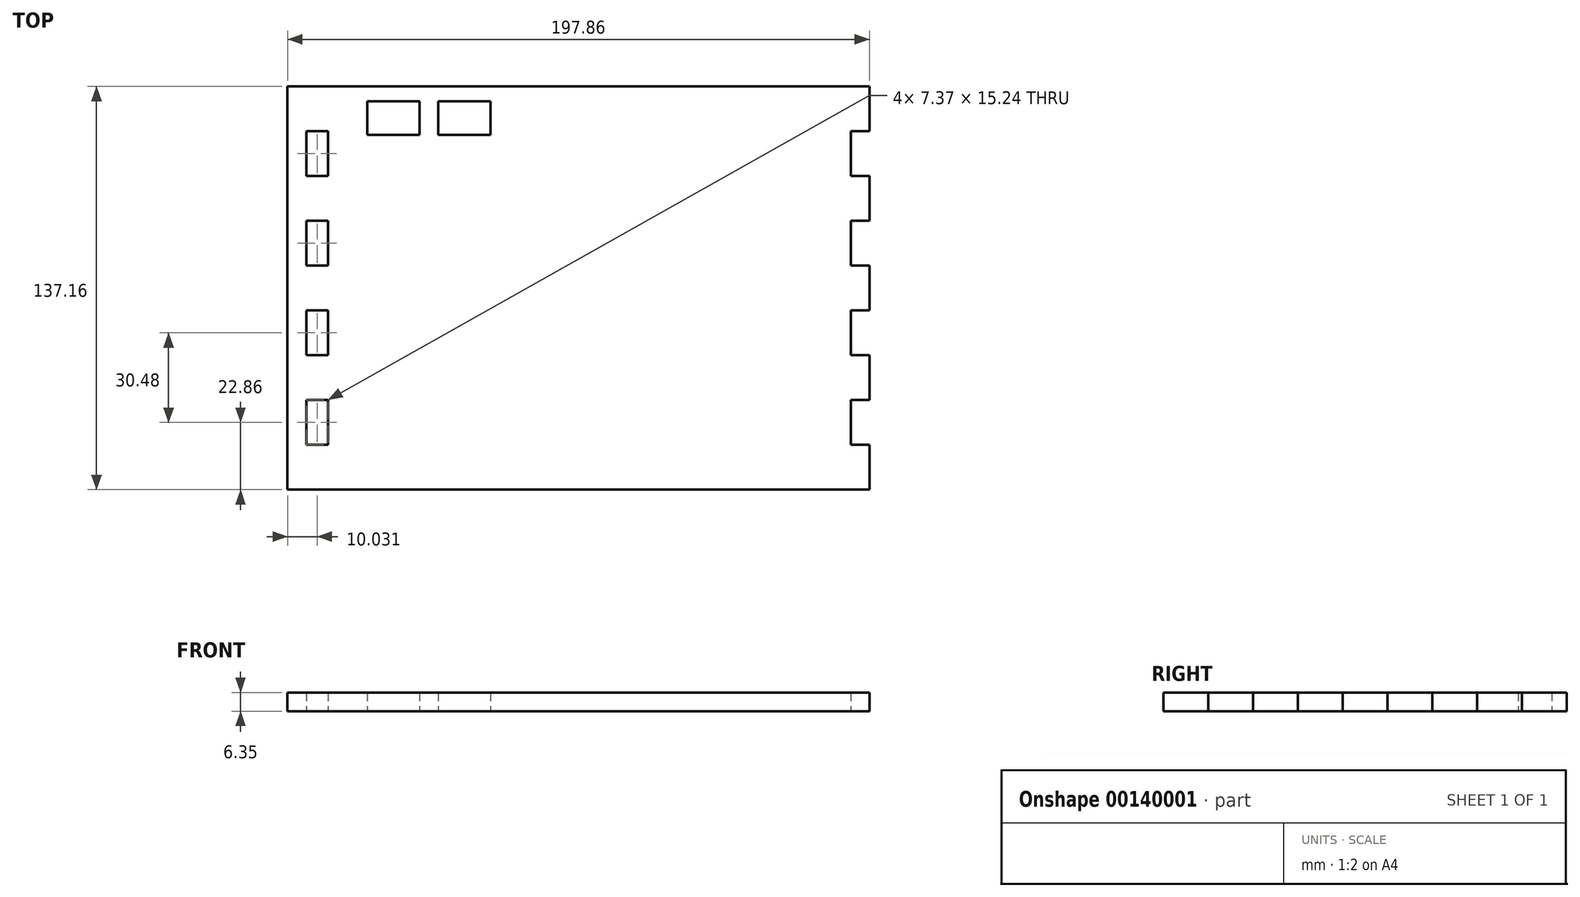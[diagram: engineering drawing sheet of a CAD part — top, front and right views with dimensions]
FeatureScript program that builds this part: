
annotation { "Feature Type Name" : "Feature", "Feature Type Description" : "" }
export const myFeature = defineFeature(function(context is Context, id is Id, definition is map)
    precondition{}
    {
        {
            var Q0;
            Q0=qCreatedBy(makeId("Top.planeOp"),FACE);
            var sketch = newSketch(context, id + "F0", { "sketchPlane" : qUnion([Q0])});
            skLineSegment(sketch, "E0.bottom", {"start": v(-69.3, 76.2) * mm, "end": v(108.5, 76.2) * mm});
            skLineSegment(sketch, "E0.top", {"start": v(-69.3, -60.96) * mm, "end": v(108.46, -60.96) * mm});
            skLineSegment(sketch, "E1", {"start": v(-76.67, 60.96) * mm, "end": v(-69.3, 60.96) * mm});
            skLineSegment(sketch, "E2", {"start": v(-69.3, 60.96) * mm, "end": v(-69.3, 45.72) * mm});
            skLineSegment(sketch, "E3", {"start": v(-69.3, 45.72) * mm, "end": v(-76.67, 45.72) * mm});
            skLineSegment(sketch, "E4", {"start": v(-76.67, 30.48) * mm, "end": v(-69.3, 30.48) * mm});
            skLineSegment(sketch, "E5", {"start": v(-69.3, 30.48) * mm, "end": v(-69.3, 15.24) * mm});
            skLineSegment(sketch, "E6", {"start": v(-69.3, 15.24) * mm, "end": v(-76.67, 15.24) * mm});
            skLineSegment(sketch, "E7", {"start": v(-76.67, 0) * mm, "end": v(-69.3, 0) * mm});
            skLineSegment(sketch, "E8", {"start": v(-69.3, 0) * mm, "end": v(-69.3, -15.24) * mm});
            skLineSegment(sketch, "E9", {"start": v(-69.3, -15.24) * mm, "end": v(-76.67, -15.24) * mm});
            skLineSegment(sketch, "E10", {"start": v(-76.67, -30.48) * mm, "end": v(-69.3, -30.48) * mm});
            skLineSegment(sketch, "E11", {"start": v(-69.3, -30.48) * mm, "end": v(-69.3, -45.72) * mm});
            skLineSegment(sketch, "E12", {"start": v(-69.3, -45.72) * mm, "end": v(-76.67, -45.72) * mm});
            skLineSegment(sketch, "E13", {"start": v(108.5, 76.2) * mm, "end": v(114.84, 76.2) * mm});
            skLineSegment(sketch, "E14", {"start": v(114.84, 76.2) * mm, "end": v(114.84, 60.96) * mm});
            skLineSegment(sketch, "E15", {"start": v(114.84, 60.96) * mm, "end": v(108.5, 60.96) * mm});
            skLineSegment(sketch, "E16", {"start": v(108.5, 60.96) * mm, "end": v(108.5, 45.72) * mm});
            skLineSegment(sketch, "E17", {"start": v(108.5, 45.72) * mm, "end": v(114.84, 45.72) * mm});
            skLineSegment(sketch, "E18", {"start": v(114.84, 45.72) * mm, "end": v(114.84, 30.48) * mm});
            skLineSegment(sketch, "E19", {"start": v(114.84, 30.48) * mm, "end": v(108.5, 30.48) * mm});
            skLineSegment(sketch, "E20", {"start": v(108.5, 30.48) * mm, "end": v(108.5, 15.24) * mm});
            skLineSegment(sketch, "E21", {"start": v(108.5, 15.24) * mm, "end": v(114.84, 15.24) * mm});
            skLineSegment(sketch, "E22", {"start": v(114.84, 15.24) * mm, "end": v(114.84, 0) * mm});
            skLineSegment(sketch, "E23", {"start": v(114.84, 0) * mm, "end": v(108.5, 0) * mm});
            skLineSegment(sketch, "E24", {"start": v(108.5, 0) * mm, "end": v(108.5, -15.24) * mm});
            skLineSegment(sketch, "E25", {"start": v(108.5, -15.24) * mm, "end": v(114.84, -15.24) * mm});
            skLineSegment(sketch, "E26", {"start": v(114.84, -15.24) * mm, "end": v(114.84, -30.48) * mm});
            skLineSegment(sketch, "E27", {"start": v(114.84, -30.48) * mm, "end": v(108.5, -30.48) * mm});
            skLineSegment(sketch, "E28", {"start": v(108.5, -30.48) * mm, "end": v(108.5, -45.72) * mm});
            skLineSegment(sketch, "E29", {"start": v(108.5, -45.72) * mm, "end": v(114.84, -45.72) * mm});
            skLineSegment(sketch, "E30", {"start": v(114.84, -60.96) * mm, "end": v(108.46, -60.96) * mm});
            skLineSegment(sketch, "E31", {"start": v(-69.3, 76.2) * mm, "end": v(-76.67, 76.2) * mm});
            skLineSegment(sketch, "E32", {"start": v(-76.67, -60.96) * mm, "end": v(-69.3, -60.96) * mm});
            skLineSegment(sketch, "E33", {"start": v(114.84, -45.72) * mm, "end": v(114.84, -60.96) * mm});
            skLineSegment(sketch, "E34", {"start": v(-76.67, -60.96) * mm, "end": v(-83.02, -60.96) * mm});
            skLineSegment(sketch, "E35", {"start": v(-83.02, -60.96) * mm, "end": v(-83.02, 76.2) * mm});
            skLineSegment(sketch, "E36", {"start": v(-83.02, 76.2) * mm, "end": v(-76.67, 76.2) * mm});
            skLineSegment(sketch, "E37", {"start": v(-76.67, 60.96) * mm, "end": v(-76.67, 45.72) * mm});
            skLineSegment(sketch, "E38", {"start": v(-76.67, 30.48) * mm, "end": v(-76.67, 15.24) * mm});
            skLineSegment(sketch, "E39", {"start": v(-76.67, 0) * mm, "end": v(-76.67, -15.24) * mm});
            skLineSegment(sketch, "E40", {"start": v(-76.67, -30.48) * mm, "end": v(-76.67, -45.72) * mm});
            skLineSegment(sketch, "E41.bottom", {"start": v(-55.93, 71.12) * mm, "end": v(-38.15, 71.12) * mm});
            skLineSegment(sketch, "E41.top", {"start": v(-55.93, 59.7) * mm, "end": v(-38.15, 59.7) * mm});
            skLineSegment(sketch, "E41.left", {"start": v(-55.93, 71.12) * mm, "end": v(-55.93, 59.7) * mm});
            skLineSegment(sketch, "E41.right", {"start": v(-38.15, 71.12) * mm, "end": v(-38.15, 59.7) * mm});
            skLineSegment(sketch, "E42.bottom", {"start": v(-31.8, 71.12) * mm, "end": v(-14.02, 71.12) * mm});
            skLineSegment(sketch, "E42.top", {"start": v(-31.8, 59.7) * mm, "end": v(-14.02, 59.7) * mm});
            skLineSegment(sketch, "E42.left", {"start": v(-31.8, 71.12) * mm, "end": v(-31.8, 59.7) * mm});
            skLineSegment(sketch, "E42.right", {"start": v(-14.02, 71.12) * mm, "end": v(-14.02, 59.7) * mm});
            skSolve(sketch);
        }
        {
            var Q0;
            Q0=makeQuery(id+"F0.imprint","IMPRINT",FACE,{"disambiguationData":[TD([[makeQuery(id+"F0.imprint","IMPRINT",EDGE,{"derivedFrom":sQuery(id+"F0.wireOp",EDGE,"E0.bottom")}),-1.0]])]});
            extrude(context, id + "F1", {"entities" : qUnion([Q0]), "depth" : 6.35 * mm});
        }
    });
